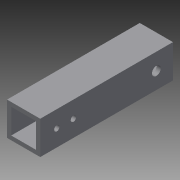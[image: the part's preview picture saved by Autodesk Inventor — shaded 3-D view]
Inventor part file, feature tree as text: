
AUTODESK INVENTOR PART (.ipt)
format: ipt  version: 2014 (Build 180170000, 170)  size: 94,720 bytes
history: native  units: in
note: dims shown in document units (in); Inventor stores cm internally (conversion verified against a paired STEP export)
features: extrude x2, sketch x2
ambient origin geometry x8: Origin, YZ Plane, XZ Plane, XY Plane, X Axis, Y Axis, Z Axis, Center Point
bodies: Solid1 (feature_tree)
feature tree (4):
  extrude  "Extrusion1"  Depth=1.0in
  extrude  "Extrusion2"  Depth=4.0in TaperAngle=0.0deg
  sketch  "Sketch1"  dims[d0=1.0in d1=1.0in]
  sketch  "Sketch2"  dims[d2=0.125in d3=4.0in d4=0.0in d5=0.163in d6=0.5in d7=0.5in d8=0.7874in d10=0.5in d11=0.3937in d13=1.0in d15=0.266in d16=0.5in d17=0.5in d18=4.0in d19=0.0in]
